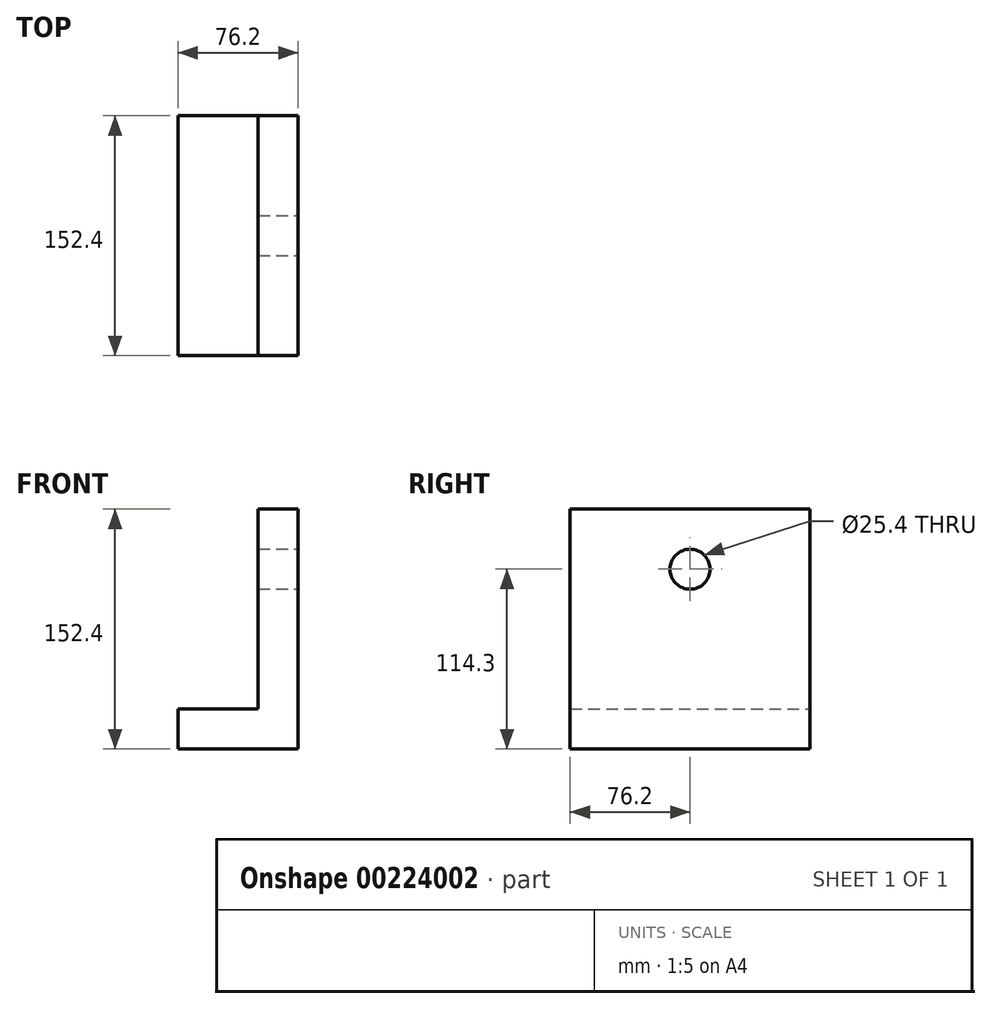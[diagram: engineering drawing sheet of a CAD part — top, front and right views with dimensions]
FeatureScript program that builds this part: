
annotation { "Feature Type Name" : "Feature", "Feature Type Description" : "" }
export const myFeature = defineFeature(function(context is Context, id is Id, definition is map)
    precondition{}
    {
        {
            var Q0;
            Q0=qCreatedBy(makeId("Front.planeOp"),FACE);
            var sketch = newSketch(context, id + "F0", { "sketchPlane" : qUnion([Q0])});
            skLineSegment(sketch, "E0", {"start": v(0, 0) * mm, "end": v(-76.2, 0) * mm});
            skLineSegment(sketch, "E1", {"start": v(0, 0) * mm, "end": v(0, 152.4) * mm});
            skLineSegment(sketch, "E2", {"start": v(-76.2, 0) * mm, "end": v(-76.2, 25.4) * mm});
            skLineSegment(sketch, "E3", {"start": v(0, 152.4) * mm, "end": v(-25.4, 152.4) * mm});
            skLineSegment(sketch, "E4", {"start": v(-76.2, 25.4) * mm, "end": v(-25.4, 25.4) * mm});
            skLineSegment(sketch, "E5", {"start": v(-25.4, 152.4) * mm, "end": v(-25.4, 25.4) * mm});
            skSolve(sketch);
        }
        {
            var Q0;
            Q0=makeQuery(id+"F0.imprint","IMPRINT",FACE,{"disambiguationData":[TD([[makeQuery(id+"F0.imprint","IMPRINT",EDGE,{"derivedFrom":sQuery(id+"F0.wireOp",EDGE,"E0")}),-1.0]])]});
            extrude(context, id + "F1", {"entities" : qUnion([Q0]), "endBound" : BoundingType.SYMMETRIC, "depth" : 152.4 * mm});
        }
        {
            var Q0;
            Q0=makeQuery(id+"F1.opExtrude","SWEPT_FACE",FACE,{"disambiguationData":[OSD([sQuery(id+"F0.wireOp",EDGE,"E1")])]});
            var sketch = newSketch(context, id + "F2", { "sketchPlane" : qUnion([Q0])});
            skLineSegment(sketch, "E6", {"start": v(0, 152.4) * mm, "end": v(0, 114.3) * mm});
            skPoint(sketch, "E6.endSnap0", {"position": v(0, 152.4) * mm});
            skCircle(sketch, "E7", {"center": v(0, 114.3) * mm, "radius": 12.7 * mm});
            skLineSegment(sketch, "E8", {"start": v(0, 114.3) * mm, "end": v(76.2, 114.3) * mm});
            skSolve(sketch);
        }
        {
            var Q0;
            {var subQ0=sQuery(id+"F2.wireOp",EDGE,"E8");var subQ1=sQuery(id+"F2.wireOp",EDGE,"E6");var subQ2=makeQuery(id+"F2.imprint","INTERSECT",VERTEX,{"derivedFrom":[subQ1,subQ0]});Q0=makeQuery(id+"F2.imprint","IMPRINT",FACE,{"disambiguationData":[TD([[makeQuery(id+"F2.imprint","IMPRINT",EDGE,{"disambiguationData":[TD([[subQ2,1.0]])],"derivedFrom":subQ1}),-1.0]])]});}
            var Q1;
            {var subQ0=sQuery(id+"F2.wireOp",EDGE,"E8");var subQ1=sQuery(id+"F2.wireOp",EDGE,"E6");var subQ2=makeQuery(id+"F2.imprint","INTERSECT",VERTEX,{"derivedFrom":[subQ1,subQ0]});Q1=makeQuery(id+"F2.imprint","IMPRINT",FACE,{"disambiguationData":[TD([[makeQuery(id+"F2.imprint","IMPRINT",EDGE,{"disambiguationData":[TD([[subQ2,1.0]])],"derivedFrom":subQ1}),1.0]])]});}
            extrude(context, id + "F3", {"entities" : qUnion([Q0, Q1]), "operationType" : NewBodyOperationType.REMOVE, "oppositeDirection" : true, "depth" : 50.8 * mm});
        }
    });
